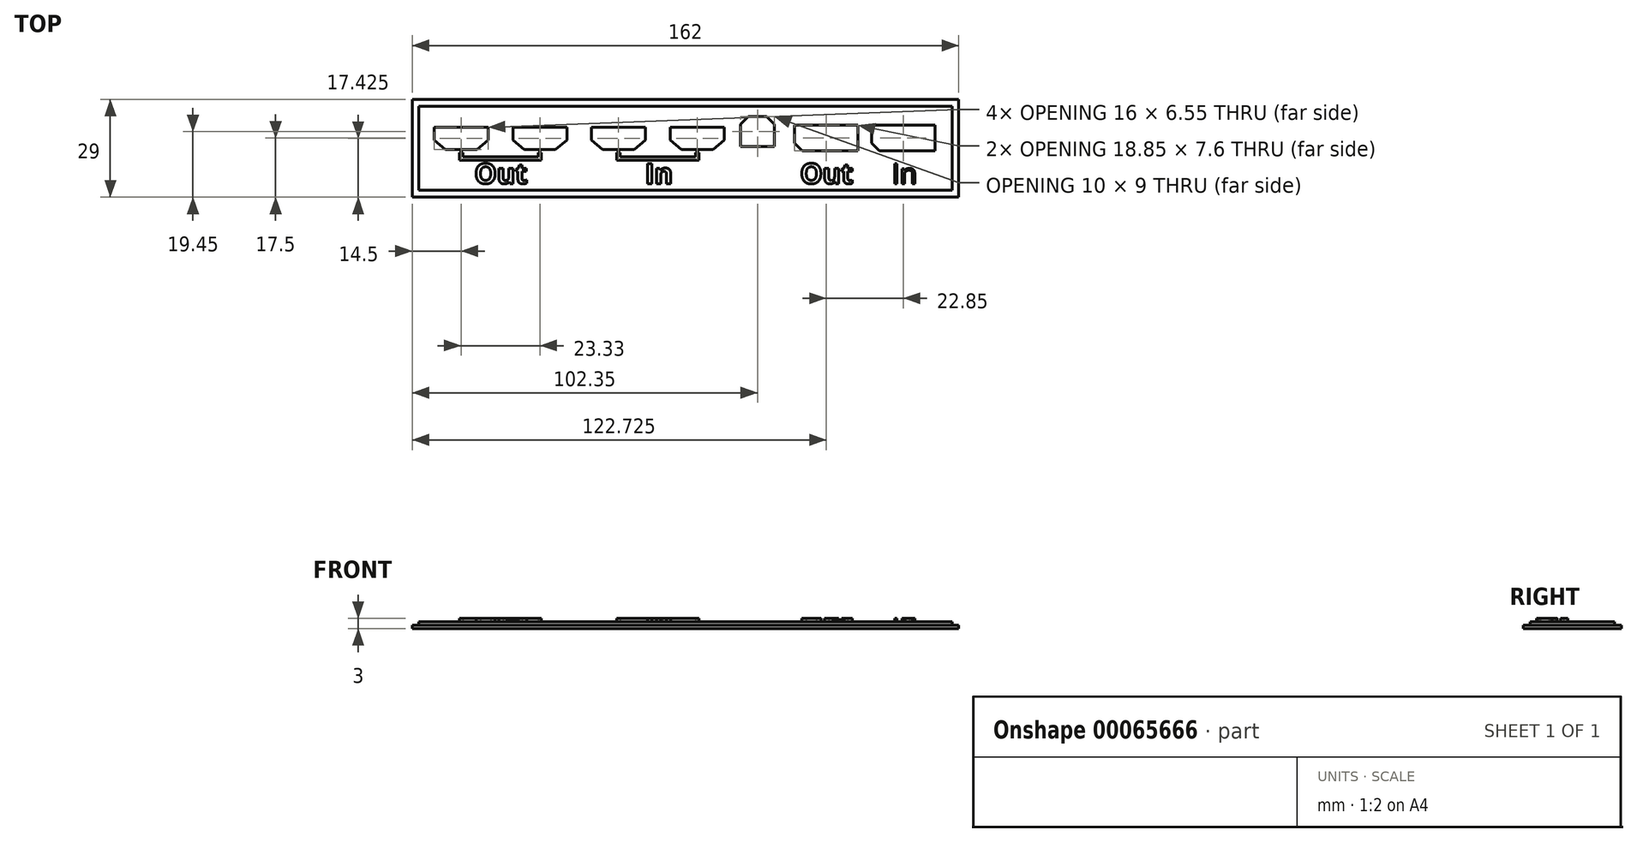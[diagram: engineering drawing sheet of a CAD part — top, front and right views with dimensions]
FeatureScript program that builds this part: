
annotation { "Feature Type Name" : "Feature", "Feature Type Description" : "" }
export const myFeature = defineFeature(function(context is Context, id is Id, definition is map)
    precondition{}
    {
        {
            assignVariable(context, id + "F0", {"name" : "flange_thickness", "anyValue" : 1});
        }
        {
            assignVariable(context, id + "F1", {"name" : "thickness", "anyValue" : 2});
        }
        {
            var Q0;
            Q0=qCreatedBy(makeId("Top.planeOp"),FACE);
            var sketch = newSketch(context, id + "F2", { "sketchPlane" : qUnion([Q0])});
            skLineSegment(sketch, "E0.bottom", {"start": v(-158, 25) * mm, "end": v(0, 25) * mm});
            skLineSegment(sketch, "E0.top", {"start": v(-158, 0) * mm, "end": v(0, 0) * mm});
            skLineSegment(sketch, "E0.left", {"start": v(-158, 25) * mm, "end": v(-158, 0) * mm});
            skLineSegment(sketch, "E0.right", {"start": v(0, 25) * mm, "end": v(0, 0) * mm});
            skLineSegment(sketch, "E1.0", {"start": v(-160, 27) * mm, "end": v(2, 27) * mm});
            skLineSegment(sketch, "E1.1", {"start": v(-160, 27) * mm, "end": v(-160, -2) * mm});
            skLineSegment(sketch, "E1.2", {"start": v(-160, -2) * mm, "end": v(2, -2) * mm});
            skLineSegment(sketch, "E1.3", {"start": v(2, 27) * mm, "end": v(2, -2) * mm});
            skSolve(sketch);
        }
        {
            var Q0;
            Q0=makeQuery(id+"F2.imprint","IMPRINT",FACE,{"disambiguationData":[TD([[makeQuery(id+"F2.imprint","IMPRINT",EDGE,{"derivedFrom":sQuery(id+"F2.wireOp",EDGE,"E0.bottom")}),-1.0]])]});
            extrude(context, id + "F3", {"entities" : qUnion([Q0]), "depth" : (getVariable(context, 'thickness')) * mm});
        }
        {
            var Q0;
            Q0=makeQuery(id+"F2.imprint","IMPRINT",FACE,{"disambiguationData":[TD([[makeQuery(id+"F2.imprint","IMPRINT",EDGE,{"derivedFrom":sQuery(id+"F2.wireOp",EDGE,"E0.bottom")}),1.0]])]});
            extrude(context, id + "F4", {"entities" : qUnion([Q0]), "operationType" : NewBodyOperationType.ADD, "depth" : (getVariable(context, 'flange_thickness')) * mm});
        }
        {
            var Q0;
            Q0=makeQuery(id+"F3.opExtrude","CAP_FACE",FACE,{"disambiguationData":[OSD([sQuery(id+"F2.wireOp",EDGE,"E0.bottom"),sQuery(id+"F2.wireOp",EDGE,"E0.top"),sQuery(id+"F2.wireOp",EDGE,"E0.left"),sQuery(id+"F2.wireOp",EDGE,"E0.right")])],"isStart":false});
            var sketch = newSketch(context, id + "F5", { "sketchPlane" : qUnion([Q0])});
            skLineSegment(sketch, "E2", {"start": v(-158, 10.2) * mm, "end": v(0, 10.2) * mm, "construction": true});
            skSolve(sketch);
        }
        {
            var Q0;
            Q0=makeQuery(id+"F3.opExtrude","CAP_FACE",FACE,{"disambiguationData":[OSD([sQuery(id+"F2.wireOp",EDGE,"E0.bottom"),sQuery(id+"F2.wireOp",EDGE,"E0.top"),sQuery(id+"F2.wireOp",EDGE,"E0.left"),sQuery(id+"F2.wireOp",EDGE,"E0.right")])],"isStart":false});
            var sketch = newSketch(context, id + "F6", { "sketchPlane" : qUnion([Q0])});
            skLineSegment(sketch, "E3", {"start": v(-145.5, 18.2) * mm, "end": v(-153, 18.2) * mm});
            skLineSegment(sketch, "E4", {"start": v(-153, 18.2) * mm, "end": v(-153, 15.2) * mm});
            skLineSegment(sketch, "E5", {"start": v(-153, 15.2) * mm, "end": v(-150, 12.65) * mm});
            skLineSegment(sketch, "E6", {"start": v(-150, 12.65) * mm, "end": v(-145.5, 12.65) * mm});
            skLineSegment(sketch, "E7", {"start": v(-145.5, 18.2) * mm, "end": v(-145.5, 12.65) * mm, "construction": true});
            skLineSegment(sketch, "E8.MirrorCS", {"start": v(-145.5, 18.2) * mm, "end": v(-138, 18.2) * mm});
            skLineSegment(sketch, "E9.MirrorCS", {"start": v(-138, 18.2) * mm, "end": v(-138, 15.2) * mm});
            skLineSegment(sketch, "E10.MirrorCS", {"start": v(-138, 15.2) * mm, "end": v(-141, 12.65) * mm});
            skLineSegment(sketch, "E11.MirrorCS", {"start": v(-141, 12.65) * mm, "end": v(-145.5, 12.65) * mm});
            skLineSegment(sketch, "E12.1.0.0", {"start": v(-122.17, 18.2) * mm, "end": v(-114.67, 18.2) * mm});
            skLineSegment(sketch, "E12.1.0.1", {"start": v(-122.17, 18.2) * mm, "end": v(-129.67, 18.2) * mm});
            skLineSegment(sketch, "E12.1.0.2", {"start": v(-129.67, 18.2) * mm, "end": v(-129.67, 15.2) * mm});
            skLineSegment(sketch, "E12.1.0.3", {"start": v(-129.67, 15.2) * mm, "end": v(-126.67, 12.65) * mm});
            skLineSegment(sketch, "E12.1.0.4", {"start": v(-126.67, 12.65) * mm, "end": v(-122.17, 12.65) * mm});
            skLineSegment(sketch, "E12.1.0.5", {"start": v(-117.67, 12.65) * mm, "end": v(-122.17, 12.65) * mm});
            skLineSegment(sketch, "E12.1.0.6", {"start": v(-114.67, 15.2) * mm, "end": v(-117.67, 12.65) * mm});
            skLineSegment(sketch, "E12.1.0.7", {"start": v(-114.67, 18.2) * mm, "end": v(-114.67, 15.2) * mm});
            skLineSegment(sketch, "E12.2.0.0", {"start": v(-98.84, 18.2) * mm, "end": v(-91.34, 18.2) * mm});
            skLineSegment(sketch, "E12.2.0.1", {"start": v(-98.84, 18.2) * mm, "end": v(-106.34, 18.2) * mm});
            skLineSegment(sketch, "E12.2.0.2", {"start": v(-106.34, 18.2) * mm, "end": v(-106.34, 15.2) * mm});
            skLineSegment(sketch, "E12.2.0.3", {"start": v(-106.34, 15.2) * mm, "end": v(-103.34, 12.65) * mm});
            skLineSegment(sketch, "E12.2.0.4", {"start": v(-103.34, 12.65) * mm, "end": v(-98.84, 12.65) * mm});
            skLineSegment(sketch, "E12.2.0.5", {"start": v(-94.34, 12.65) * mm, "end": v(-98.84, 12.65) * mm});
            skLineSegment(sketch, "E12.2.0.6", {"start": v(-91.34, 15.2) * mm, "end": v(-94.34, 12.65) * mm});
            skLineSegment(sketch, "E12.2.0.7", {"start": v(-91.34, 18.2) * mm, "end": v(-91.34, 15.2) * mm});
            skLineSegment(sketch, "E12.3.0.0", {"start": v(-75.5, 18.2) * mm, "end": v(-68, 18.2) * mm});
            skLineSegment(sketch, "E12.3.0.1", {"start": v(-75.5, 18.2) * mm, "end": v(-83.01, 18.2) * mm});
            skLineSegment(sketch, "E12.3.0.2", {"start": v(-83.01, 18.2) * mm, "end": v(-83.01, 15.2) * mm});
            skLineSegment(sketch, "E12.3.0.3", {"start": v(-83.01, 15.2) * mm, "end": v(-80, 12.65) * mm});
            skLineSegment(sketch, "E12.3.0.4", {"start": v(-80, 12.65) * mm, "end": v(-75.5, 12.65) * mm});
            skLineSegment(sketch, "E12.3.0.5", {"start": v(-71, 12.65) * mm, "end": v(-75.5, 12.65) * mm});
            skLineSegment(sketch, "E12.3.0.6", {"start": v(-68, 15.2) * mm, "end": v(-71, 12.65) * mm});
            skLineSegment(sketch, "E12.3.0.7", {"start": v(-68, 18.2) * mm, "end": v(-68, 15.2) * mm});
            skLineSegment(sketch, "E12.direction1", {"start": v(-145.5, 18.2) * mm, "end": v(-122.17, 18.2) * mm, "construction": true});
            skSolve(sketch);
        }
        {
            var Q0;
            Q0=makeQuery(id+"F3.opExtrude","CAP_FACE",FACE,{"disambiguationData":[OSD([sQuery(id+"F2.wireOp",EDGE,"E0.bottom"),sQuery(id+"F2.wireOp",EDGE,"E0.top"),sQuery(id+"F2.wireOp",EDGE,"E0.left"),sQuery(id+"F2.wireOp",EDGE,"E0.right")])],"isStart":false});
            var sketch = newSketch(context, id + "F7", { "sketchPlane" : qUnion([Q0])});
            skLineSegment(sketch, "E13.bottom", {"start": v(-63.7, 22.8) * mm, "end": v(-51.6, 22.8) * mm, "construction": true});
            skLineSegment(sketch, "E13.top", {"start": v(-63.7, 12.1) * mm, "end": v(-51.6, 12.1) * mm, "construction": true});
            skLineSegment(sketch, "E13.left", {"start": v(-63.7, 22.8) * mm, "end": v(-63.7, 12.1) * mm, "construction": true});
            skLineSegment(sketch, "E13.right", {"start": v(-51.6, 22.8) * mm, "end": v(-51.6, 12.1) * mm, "construction": true});
            skLineSegment(sketch, "E14", {"start": v(-57.65, 13.45) * mm, "end": v(-62.15, 13.45) * mm});
            skLineSegment(sketch, "E15", {"start": v(-62.15, 13.45) * mm, "end": v(-62.15, 19.45) * mm});
            skLineSegment(sketch, "E16", {"start": v(-62.15, 19.45) * mm, "end": v(-60.15, 21.45) * mm});
            skLineSegment(sketch, "E17", {"start": v(-60.15, 21.45) * mm, "end": v(-57.65, 21.45) * mm});
            skPoint(sketch, "E18", {"position": v(-57.65, 12.1) * mm});
            skLineSegment(sketch, "E19", {"start": v(-57.65, 21.45) * mm, "end": v(-57.65, 22.8) * mm, "construction": true});
            skLineSegment(sketch, "E20", {"start": v(-57.65, 13.45) * mm, "end": v(-57.65, 12.1) * mm, "construction": true});
            skLineSegment(sketch, "E21.MirrorCS", {"start": v(-57.65, 13.45) * mm, "end": v(-53.15, 13.45) * mm});
            skLineSegment(sketch, "E22.MirrorCS", {"start": v(-53.15, 13.45) * mm, "end": v(-53.15, 19.45) * mm});
            skLineSegment(sketch, "E23.MirrorCS", {"start": v(-55.15, 21.45) * mm, "end": v(-57.65, 21.45) * mm});
            skLineSegment(sketch, "E24.MirrorCS", {"start": v(-53.15, 19.45) * mm, "end": v(-55.15, 21.45) * mm});
            skSolve(sketch);
        }
        {
            var Q0;
            Q0=makeQuery(id+"F6.imprint","IMPRINT",FACE,{"disambiguationData":[TD([[makeQuery(id+"F6.imprint","IMPRINT",EDGE,{"derivedFrom":sQuery(id+"F6.wireOp",EDGE,"E3")}),-1.0]])]});
            var sketch = newSketch(context, id + "F8", { "sketchPlane" : qUnion([Q0])});
            skLineSegment(sketch, "E25", {"start": v(-5.5, 18.8) * mm, "end": v(-23.35, 18.8) * mm});
            skLineSegment(sketch, "E26", {"start": v(-23.35, 18.8) * mm, "end": v(-23.35, 14.2) * mm});
            skLineSegment(sketch, "E27", {"start": v(-23.35, 14.2) * mm, "end": v(-21.35, 12.2) * mm});
            skLineSegment(sketch, "E28", {"start": v(-21.35, 12.2) * mm, "end": v(-5.5, 12.2) * mm});
            skLineSegment(sketch, "E29", {"start": v(-5.5, 12.2) * mm, "end": v(-5.5, 18.8) * mm});
            skPoint(sketch, "E30", {"position": v(-14.43, 18.8) * mm});
            skPoint(sketch, "E31.1.0.0", {"position": v(-37.28, 18.8) * mm});
            skLineSegment(sketch, "E31.1.0.1", {"start": v(-28.35, 18.8) * mm, "end": v(-46.2, 18.8) * mm});
            skLineSegment(sketch, "E31.1.0.2", {"start": v(-46.2, 18.8) * mm, "end": v(-46.2, 14.2) * mm});
            skLineSegment(sketch, "E31.1.0.3", {"start": v(-46.2, 14.2) * mm, "end": v(-44.2, 12.2) * mm});
            skLineSegment(sketch, "E31.1.0.4", {"start": v(-44.2, 12.2) * mm, "end": v(-28.35, 12.2) * mm});
            skLineSegment(sketch, "E31.1.0.5", {"start": v(-28.35, 12.2) * mm, "end": v(-28.35, 18.8) * mm});
            skLineSegment(sketch, "E31.direction1", {"start": v(-14.43, 18.8) * mm, "end": v(-37.28, 18.8) * mm, "construction": true});
            skSolve(sketch);
        }
        {
            var Q0;
            Q0=qSketchRegion(id+"F6",true);
            var Q1;
            Q1=qSketchRegion(id+"F7",true);
            var Q2;
            Q2=qSketchRegion(id+"F8",true);
            extrude(context, id + "F9", {"entities" : qUnion([Q0, Q1, Q2]), "endBound" : BoundingType.UP_TO_NEXT, "oppositeDirection" : true, "depth" : 25 * mm});
        }
        {
            var Q0;
            Q0=makeQuery(id+"F9.opExtrude","SWEPT_BODY",BODY,{"disambiguationData":[OSD([sQuery(id+"F6.wireOp",EDGE,"E3"),sQuery(id+"F6.wireOp",EDGE,"E4"),sQuery(id+"F6.wireOp",EDGE,"E5"),sQuery(id+"F6.wireOp",EDGE,"E6"),sQuery(id+"F6.wireOp",EDGE,"E8.MirrorCS"),sQuery(id+"F6.wireOp",EDGE,"E9.MirrorCS"),sQuery(id+"F6.wireOp",EDGE,"E10.MirrorCS"),sQuery(id+"F6.wireOp",EDGE,"E11.MirrorCS")])]});
            var Q1;
            Q1=makeQuery(id+"F9.opExtrude","SWEPT_BODY",BODY,{"disambiguationData":[OSD([sQuery(id+"F6.wireOp",EDGE,"E12.1.0.0"),sQuery(id+"F6.wireOp",EDGE,"E12.1.0.1"),sQuery(id+"F6.wireOp",EDGE,"E12.1.0.2"),sQuery(id+"F6.wireOp",EDGE,"E12.1.0.3"),sQuery(id+"F6.wireOp",EDGE,"E12.1.0.4"),sQuery(id+"F6.wireOp",EDGE,"E12.1.0.5"),sQuery(id+"F6.wireOp",EDGE,"E12.1.0.6"),sQuery(id+"F6.wireOp",EDGE,"E12.1.0.7")])]});
            var Q2;
            Q2=makeQuery(id+"F9.opExtrude","SWEPT_BODY",BODY,{"disambiguationData":[OSD([sQuery(id+"F6.wireOp",EDGE,"E12.2.0.0"),sQuery(id+"F6.wireOp",EDGE,"E12.2.0.1"),sQuery(id+"F6.wireOp",EDGE,"E12.2.0.2"),sQuery(id+"F6.wireOp",EDGE,"E12.2.0.3"),sQuery(id+"F6.wireOp",EDGE,"E12.2.0.4"),sQuery(id+"F6.wireOp",EDGE,"E12.2.0.5"),sQuery(id+"F6.wireOp",EDGE,"E12.2.0.6"),sQuery(id+"F6.wireOp",EDGE,"E12.2.0.7")])]});
            var Q3;
            Q3=makeQuery(id+"F9.opExtrude","SWEPT_BODY",BODY,{"disambiguationData":[OSD([sQuery(id+"F6.wireOp",EDGE,"E12.3.0.0"),sQuery(id+"F6.wireOp",EDGE,"E12.3.0.1"),sQuery(id+"F6.wireOp",EDGE,"E12.3.0.2"),sQuery(id+"F6.wireOp",EDGE,"E12.3.0.3"),sQuery(id+"F6.wireOp",EDGE,"E12.3.0.4"),sQuery(id+"F6.wireOp",EDGE,"E12.3.0.5"),sQuery(id+"F6.wireOp",EDGE,"E12.3.0.6"),sQuery(id+"F6.wireOp",EDGE,"E12.3.0.7")])]});
            var Q4;
            Q4=makeQuery(id+"F9.opExtrude","SWEPT_BODY",BODY,{"disambiguationData":[OSD([sQuery(id+"F8.wireOp",EDGE,"E31.1.0.1"),sQuery(id+"F8.wireOp",EDGE,"E31.1.0.2"),sQuery(id+"F8.wireOp",EDGE,"E31.1.0.3"),sQuery(id+"F8.wireOp",EDGE,"E31.1.0.4"),sQuery(id+"F8.wireOp",EDGE,"E31.1.0.5")])]});
            var Q5;
            Q5=makeQuery(id+"F9.opExtrude","SWEPT_BODY",BODY,{"disambiguationData":[OSD([sQuery(id+"F7.wireOp",EDGE,"E14"),sQuery(id+"F7.wireOp",EDGE,"E15"),sQuery(id+"F7.wireOp",EDGE,"E16"),sQuery(id+"F7.wireOp",EDGE,"E17"),sQuery(id+"F7.wireOp",EDGE,"E21.MirrorCS"),sQuery(id+"F7.wireOp",EDGE,"E22.MirrorCS"),sQuery(id+"F7.wireOp",EDGE,"E23.MirrorCS"),sQuery(id+"F7.wireOp",EDGE,"E24.MirrorCS")])]});
            var Q6;
            Q6=makeQuery(id+"F9.opExtrude","SWEPT_BODY",BODY,{"disambiguationData":[OSD([sQuery(id+"F8.wireOp",EDGE,"E25"),sQuery(id+"F8.wireOp",EDGE,"E26"),sQuery(id+"F8.wireOp",EDGE,"E27"),sQuery(id+"F8.wireOp",EDGE,"E28"),sQuery(id+"F8.wireOp",EDGE,"E29")])]});
            var Q7;
            Q7=makeQuery(id+"F3.opExtrude","SWEPT_BODY",BODY,{"disambiguationData":[OSD([sQuery(id+"F2.wireOp",EDGE,"E0.bottom"),sQuery(id+"F2.wireOp",EDGE,"E0.top"),sQuery(id+"F2.wireOp",EDGE,"E0.left"),sQuery(id+"F2.wireOp",EDGE,"E0.right")])]});
            booleanBodies(context, id + "F10", {"operationType" : BooleanOperationType.SUBTRACTION, "tools" : qUnion([Q0, Q1, Q2, Q3, Q4, Q5, Q6]), "targets" : qUnion([Q7]), "offset" : true, "offsetAll" : true, "offsetDistance" : 0.5 * mm});
        }
        {
            var Q0;
            Q0=makeQuery(id+"F3.opExtrude","CAP_FACE",FACE,{"disambiguationData":[OSD([sQuery(id+"F2.wireOp",EDGE,"E0.bottom"),sQuery(id+"F2.wireOp",EDGE,"E0.top"),sQuery(id+"F2.wireOp",EDGE,"E0.left"),sQuery(id+"F2.wireOp",EDGE,"E0.right")])],"isStart":false});
            var sketch = newSketch(context, id + "F11", { "sketchPlane" : qUnion([Q0])});
            skText(sketch, "E32", { "text": "In", "fontName": "OpenSans-Bold.ttf"});
            skLineSegment(sketch, "E33", {"start": v(-90.84, 18.7) * mm, "end": v(-83.51, 18.7) * mm, "construction": true});
            skPoint(sketch, "E34", {"position": v(-87.17, 18.7) * mm});
            skText(sketch, "E35", { "text": "Out", "fontName": "OpenSans-Bold.ttf"});
            skLineSegment(sketch, "E36", {"start": v(-137.5, 18.7) * mm, "end": v(-130.17, 18.7) * mm, "construction": true});
            skPoint(sketch, "E37", {"position": v(-133.83, 18.7) * mm});
            skLineSegment(sketch, "E38", {"start": v(-158, 2) * mm, "end": v(0, 2) * mm, "construction": true});
            skPoint(sketch, "E39", {"position": v(-57.65, 12.95) * mm});
            skText(sketch, "E40", { "text": "Out", "fontName": "OpenSans-Bold.ttf"});
            skText(sketch, "E41", { "text": "In", "fontName": "OpenSans-Regular.ttf"});
            skPoint(sketch, "E42", {"position": v(-37.28, 19.3) * mm});
            skPoint(sketch, "E43", {"position": v(-14.43, 19.3) * mm});
            skPoint(sketch, "E44", {"position": v(-145.5, 18.7) * mm});
            skPoint(sketch, "E45", {"position": v(-122.17, 18.7) * mm});
            skLineSegment(sketch, "E46.top", {"start": v(-146, 8.96) * mm, "end": v(-133.83, 8.96) * mm});
            skLineSegment(sketch, "E47", {"start": v(-146, 8.96) * mm, "end": v(-146, 11.23) * mm});
            skLineSegment(sketch, "E48", {"start": v(-146, 11.23) * mm, "end": v(-145, 11.23) * mm});
            skLineSegment(sketch, "E49", {"start": v(-145, 11.23) * mm, "end": v(-145, 9.96) * mm});
            skLineSegment(sketch, "E50", {"start": v(-145, 9.96) * mm, "end": v(-133.83, 9.96) * mm});
            skLineSegment(sketch, "E51", {"start": v(-133.83, 9.96) * mm, "end": v(-133.83, 8.96) * mm, "construction": true});
            skPoint(sketch, "E52", {"position": v(-145.5, 11.23) * mm});
            skLineSegment(sketch, "E53.MirrorCS", {"start": v(-121.67, 11.23) * mm, "end": v(-122.67, 11.23) * mm});
            skLineSegment(sketch, "E54.MirrorCS", {"start": v(-122.67, 11.23) * mm, "end": v(-122.67, 9.96) * mm});
            skLineSegment(sketch, "E55.MirrorCS", {"start": v(-121.67, 8.96) * mm, "end": v(-121.67, 11.23) * mm});
            skLineSegment(sketch, "E56.MirrorCS", {"start": v(-122.67, 9.96) * mm, "end": v(-133.83, 9.96) * mm});
            skLineSegment(sketch, "E57.MirrorCS", {"start": v(-121.67, 8.96) * mm, "end": v(-133.83, 8.96) * mm});
            skLineSegment(sketch, "E58", {"start": v(-114.17, 18.7) * mm, "end": v(-106.84, 18.7) * mm, "construction": true});
            skLineSegment(sketch, "E59", {"start": v(-110.5, 18.7) * mm, "end": v(-110.5, 2) * mm, "construction": true});
            skLineSegment(sketch, "E60.MirrorCS", {"start": v(-76, 11.23) * mm, "end": v(-76, 9.96) * mm});
            skLineSegment(sketch, "E61.MirrorCS", {"start": v(-75, 11.23) * mm, "end": v(-76, 11.23) * mm});
            skPoint(sketch, "E62.MirrorP", {"position": v(-75.5, 11.23) * mm});
            skLineSegment(sketch, "E63.MirrorCS", {"start": v(-75, 8.96) * mm, "end": v(-75, 11.23) * mm});
            skLineSegment(sketch, "E64.MirrorCS", {"start": v(-99.34, 11.23) * mm, "end": v(-98.34, 11.23) * mm});
            skLineSegment(sketch, "E65.MirrorCS", {"start": v(-75, 8.96) * mm, "end": v(-87.17, 8.96) * mm});
            skLineSegment(sketch, "E66.MirrorCS", {"start": v(-99.34, 8.96) * mm, "end": v(-99.34, 11.23) * mm});
            skLineSegment(sketch, "E67.MirrorCS", {"start": v(-98.34, 9.96) * mm, "end": v(-87.17, 9.96) * mm});
            skLineSegment(sketch, "E68.MirrorCS", {"start": v(-76, 9.96) * mm, "end": v(-87.17, 9.96) * mm});
            skLineSegment(sketch, "E69.MirrorCS", {"start": v(-99.34, 8.96) * mm, "end": v(-87.17, 8.96) * mm});
            skLineSegment(sketch, "E70.MirrorCS", {"start": v(-98.34, 11.23) * mm, "end": v(-98.34, 9.96) * mm});
            const initialGuessF11  = {"E32": [-0.09098, 0.002, 1, 0, 0.006], "E35": [-0.14156, 0.002, 1, 0, 0.006], "E40": [-0.045, 0.002, 1, 0, 0.006], "E41": [-0.0178, 0.002, 1, 0, 0.006]};
            skSetInitialGuess(sketch, initialGuessF11);
            skSolve(sketch);
        }
        {
            var Q0;
            Q0=qSketchRegion(id+"F11",true);
            extrude(context, id + "F12", {"entities" : qUnion([Q0]), "operationType" : NewBodyOperationType.ADD, "depth" : 1 * mm});
        }
    });
